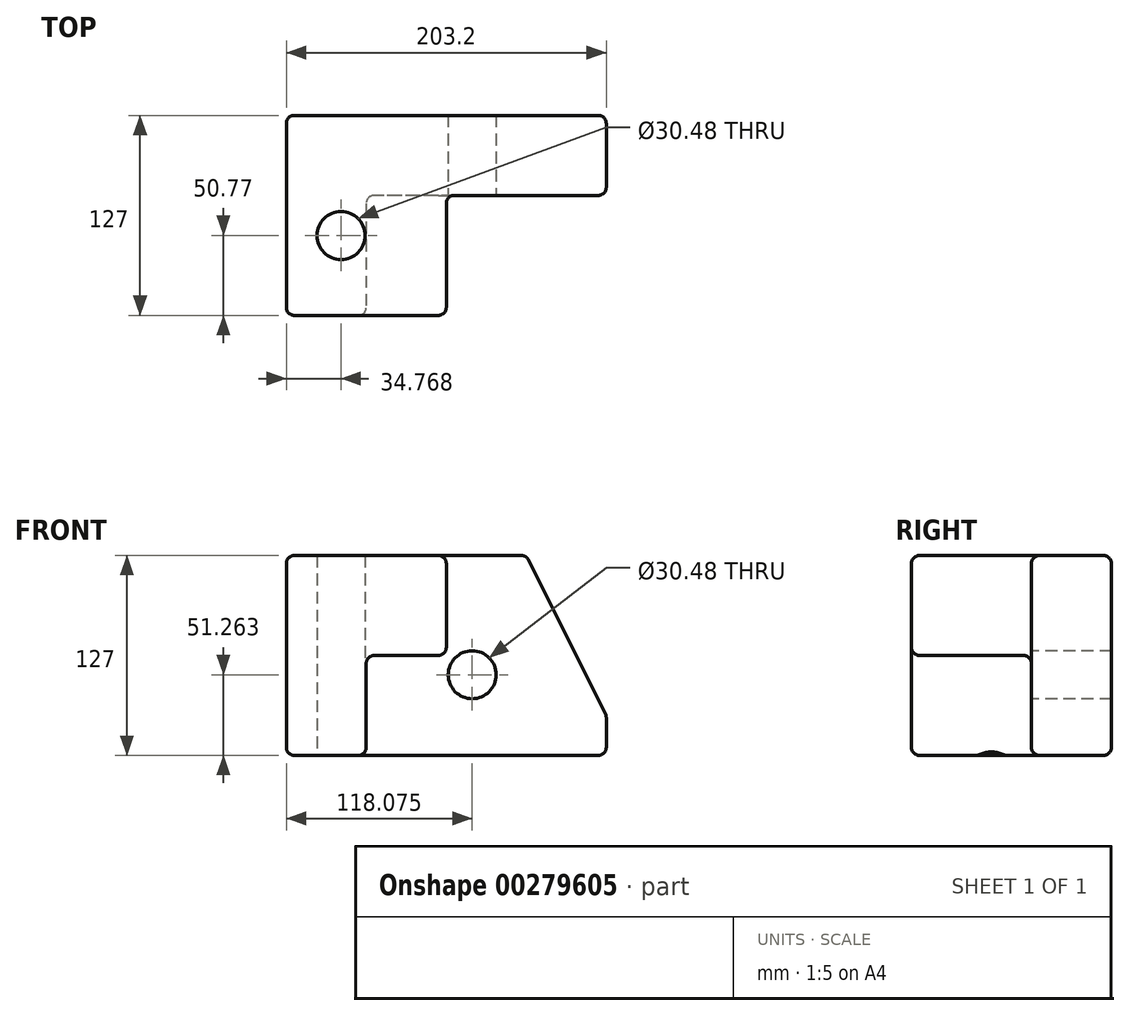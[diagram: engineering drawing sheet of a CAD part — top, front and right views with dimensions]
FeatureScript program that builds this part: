
annotation { "Feature Type Name" : "Feature", "Feature Type Description" : "" }
export const myFeature = defineFeature(function(context is Context, id is Id, definition is map)
    precondition{}
    {
        {
            var Q0;
            Q0=qCreatedBy(makeId("Front.planeOp"),FACE);
            var sketch = newSketch(context, id + "F0", { "sketchPlane" : qUnion([Q0])});
            skLineSegment(sketch, "E0.bottom", {"start": v(101.6, 63.5) * mm, "end": v(-101.6, 63.5) * mm});
            skLineSegment(sketch, "E0.top", {"start": v(101.6, -63.5) * mm, "end": v(-101.6, -63.5) * mm});
            skLineSegment(sketch, "E0.left", {"start": v(101.6, 63.5) * mm, "end": v(101.6, -63.5) * mm});
            skLineSegment(sketch, "E0.right", {"start": v(-101.6, 63.5) * mm, "end": v(-101.6, -63.5) * mm});
            skPoint(sketch, "E0.middle", {"position": v(0, 0) * mm});
            skSolve(sketch);
        }
        {
            var Q0;
            Q0=makeQuery(id+"F0.imprint","IMPRINT",FACE,{"disambiguationData":[TD([[makeQuery(id+"F0.imprint","IMPRINT",EDGE,{"derivedFrom":sQuery(id+"F0.wireOp",EDGE,"E0.bottom")}),1.0]])]});
            extrude(context, id + "F1", {"entities" : qUnion([Q0]), "depth" : 127 * mm});
        }
        {
            var Q0;
            Q0=makeQuery(id+"F1.opExtrude","CAP_FACE",FACE,{"disambiguationData":[OSD([sQuery(id+"F0.wireOp",EDGE,"E0.bottom"),sQuery(id+"F0.wireOp",EDGE,"E0.top"),sQuery(id+"F0.wireOp",EDGE,"E0.left"),sQuery(id+"F0.wireOp",EDGE,"E0.right")])],"isStart":false});
            var sketch = newSketch(context, id + "F2", { "sketchPlane" : qUnion([Q0])});
            skLineSegment(sketch, "E1", {"start": v(0, 63.5) * mm, "end": v(0, 0) * mm});
            skLineSegment(sketch, "E2", {"start": v(0, 0) * mm, "end": v(-50.83, 0) * mm});
            skLineSegment(sketch, "E3", {"start": v(-50.83, 0) * mm, "end": v(-50.83, -63.5) * mm});
            skSolve(sketch);
        }
        {
            var Q0;
            Q0 = qSketchRegion(id + "F2", true);
            var Q1;
            {var subQ2=sQuery(id+"F2.wireOp",EDGE,"E1");Q1=makeQuery(id+"F2.imprint","IMPRINT",FACE,{"disambiguationData":[TD([[makeQuery(id+"F2.imprint","IMPRINT",EDGE,{"derivedFrom":subQ2}),1.0]])]});}
            extrude(context, id + "F3", {"entities" : qUnion([Q0, Q1]), "operationType" : NewBodyOperationType.REMOVE, "oppositeDirection" : true, "depth" : 76.2 * mm});
        }
        {
            var Q0;
            Q0=makeQuery(id+"F1.opExtrude","SWEPT_EDGE",EDGE,{"disambiguationData":[OSD([sQuery(id+"F0.wireOp",EDGE,"E0.bottom"),sQuery(id+"F0.wireOp",EDGE,"E0.left")])]});
            chamfer(context, id + "F4", {"entities" : qUnion([Q0]), "chamferType" : ChamferType.TWO_OFFSETS, "width1" : 50.8 * mm, "oppositeDirection" : false, "width2" : 101.6 * mm, "tangentPropagation" : true});
        }
        {
            var Q0;
            Q0=makeQuery(id+"F1.opExtrude","SWEPT_FACE",FACE,{"disambiguationData":[OSD([sQuery(id+"F0.wireOp",EDGE,"E0.bottom")])]});
            var Q1;
            Q1=makeQuery(id+"F1.opExtrude","CAP_FACE",FACE,{"disambiguationData":[OSD([sQuery(id+"F0.wireOp",EDGE,"E0.bottom"),sQuery(id+"F0.wireOp",EDGE,"E0.top"),sQuery(id+"F0.wireOp",EDGE,"E0.left"),sQuery(id+"F0.wireOp",EDGE,"E0.right")])],"isStart":false});
            var Q2;
            Q2=makeQuery(id+"F3.boolean.opBoolean","COPY",FACE,{"derivedFrom":makeQuery(id+"F3.opExtrude","SWEPT_FACE",FACE,{"disambiguationData":[OSD([sQuery(id+"F2.wireOp",EDGE,"E1")])]})});
            var Q3;
            Q3=makeQuery(id+"F3.boolean.opBoolean","COPY",FACE,{"derivedFrom":makeQuery(id+"F3.opExtrude","SWEPT_FACE",FACE,{"disambiguationData":[OSD([sQuery(id+"F2.wireOp",EDGE,"E3")])]})});
            var Q4;
            Q4=makeQuery(id+"F3.boolean.opBoolean","COPY",FACE,{"derivedFrom":makeQuery(id+"F3.opExtrude","CAP_FACE",FACE,{"disambiguationData":[OSD([sQuery(id+"F0.wireOp",EDGE,"E0.bottom"),sQuery(id+"F0.wireOp",EDGE,"E0.top"),sQuery(id+"F0.wireOp",EDGE,"E0.left"),sQuery(id+"F2.wireOp",EDGE,"E1"),sQuery(id+"F2.wireOp",EDGE,"E2"),sQuery(id+"F2.wireOp",EDGE,"E3")])],"isStart":false})});
            var Q5;
            Q5=makeQuery(id+"F4.opChamfer","BLEND_FACE",FACE,{"disambiguationData":[OSD([sQuery(id+"F0.wireOp",EDGE,"E0.bottom"),sQuery(id+"F0.wireOp",EDGE,"E0.left")])]});
            var Q6;
            Q6=makeQuery(id+"F1.opExtrude","SWEPT_FACE",FACE,{"disambiguationData":[OSD([sQuery(id+"F0.wireOp",EDGE,"E0.left")])]});
            var Q7;
            Q7=makeQuery(id+"F1.opExtrude","SWEPT_FACE",FACE,{"disambiguationData":[OSD([sQuery(id+"F0.wireOp",EDGE,"E0.right")])]});
            var Q8;
            Q8=makeQuery(id+"F1.opExtrude","CAP_FACE",FACE,{"disambiguationData":[OSD([sQuery(id+"F0.wireOp",EDGE,"E0.bottom"),sQuery(id+"F0.wireOp",EDGE,"E0.top"),sQuery(id+"F0.wireOp",EDGE,"E0.left"),sQuery(id+"F0.wireOp",EDGE,"E0.right")])],"isStart":true});
            fillet(context, id + "F5", {"entities" : qUnion([Q0, Q1, Q2, Q3, Q4, Q5, Q6, Q7, Q8]), "radius" : 5.08 * mm, "tangentPropagation" : true, "allowEdgeOverflow" : false});
        }
        {
            var Q0;
            Q0=makeQuery(id+"F3.boolean.opBoolean","COPY",FACE,{"derivedFrom":makeQuery(id+"F3.opExtrude","CAP_FACE",FACE,{"disambiguationData":[OSD([sQuery(id+"F0.wireOp",EDGE,"E0.bottom"),sQuery(id+"F0.wireOp",EDGE,"E0.top"),sQuery(id+"F0.wireOp",EDGE,"E0.left"),sQuery(id+"F2.wireOp",EDGE,"E1"),sQuery(id+"F2.wireOp",EDGE,"E2"),sQuery(id+"F2.wireOp",EDGE,"E3")])],"isStart":false})});
            var sketch = newSketch(context, id + "F6", { "sketchPlane" : qUnion([Q0])});
            skLineSegment(sketch, "E4", {"start": v(-45.75, -39.77) * mm, "end": v(5.05, -39.77) * mm});
            skCircle(sketch, "E5", {"center": v(16.48, -12.24) * mm, "radius": 15.24 * mm});
            skSolve(sketch);
        }
        {
            var Q0;
            Q0=makeQuery(id+"F6.imprint","IMPRINT",FACE,{"disambiguationData":[TD([[makeQuery(id+"F6.imprint","IMPRINT",EDGE,{"derivedFrom":sQuery(id+"F6.wireOp",EDGE,"E5")}),1.0]])]});
            extrude(context, id + "F7", {"entities" : qUnion([Q0]), "operationType" : NewBodyOperationType.REMOVE, "oppositeDirection" : true, "depth" : 101.6 * mm, "hasSecondDirection" : true, "secondDirectionOppositeDirection" : false, "secondDirectionDepth" : 101.6 * mm});
        }
        {
            var Q0;
            Q0=makeQuery(id+"F1.opExtrude","SWEPT_FACE",FACE,{"disambiguationData":[OSD([sQuery(id+"F0.wireOp",EDGE,"E0.bottom")])]});
            var sketch = newSketch(context, id + "F8", { "sketchPlane" : qUnion([Q0])});
            skCircle(sketch, "E6", {"center": v(-66.83, -76.23) * mm, "radius": 15.24 * mm});
            skSolve(sketch);
        }
        {
            var Q0;
            Q0=makeQuery(id+"F8.imprint","IMPRINT",FACE,{"disambiguationData":[TD([[makeQuery(id+"F8.imprint","IMPRINT",EDGE,{"derivedFrom":sQuery(id+"F8.wireOp",EDGE,"E6")}),1.0]])]});
            extrude(context, id + "F9", {"entities" : qUnion([Q0]), "operationType" : NewBodyOperationType.REMOVE, "depth" : 127 * mm, "hasSecondDirection" : true, "secondDirectionOppositeDirection" : true, "secondDirectionDepth" : 127 * mm});
        }
    });
